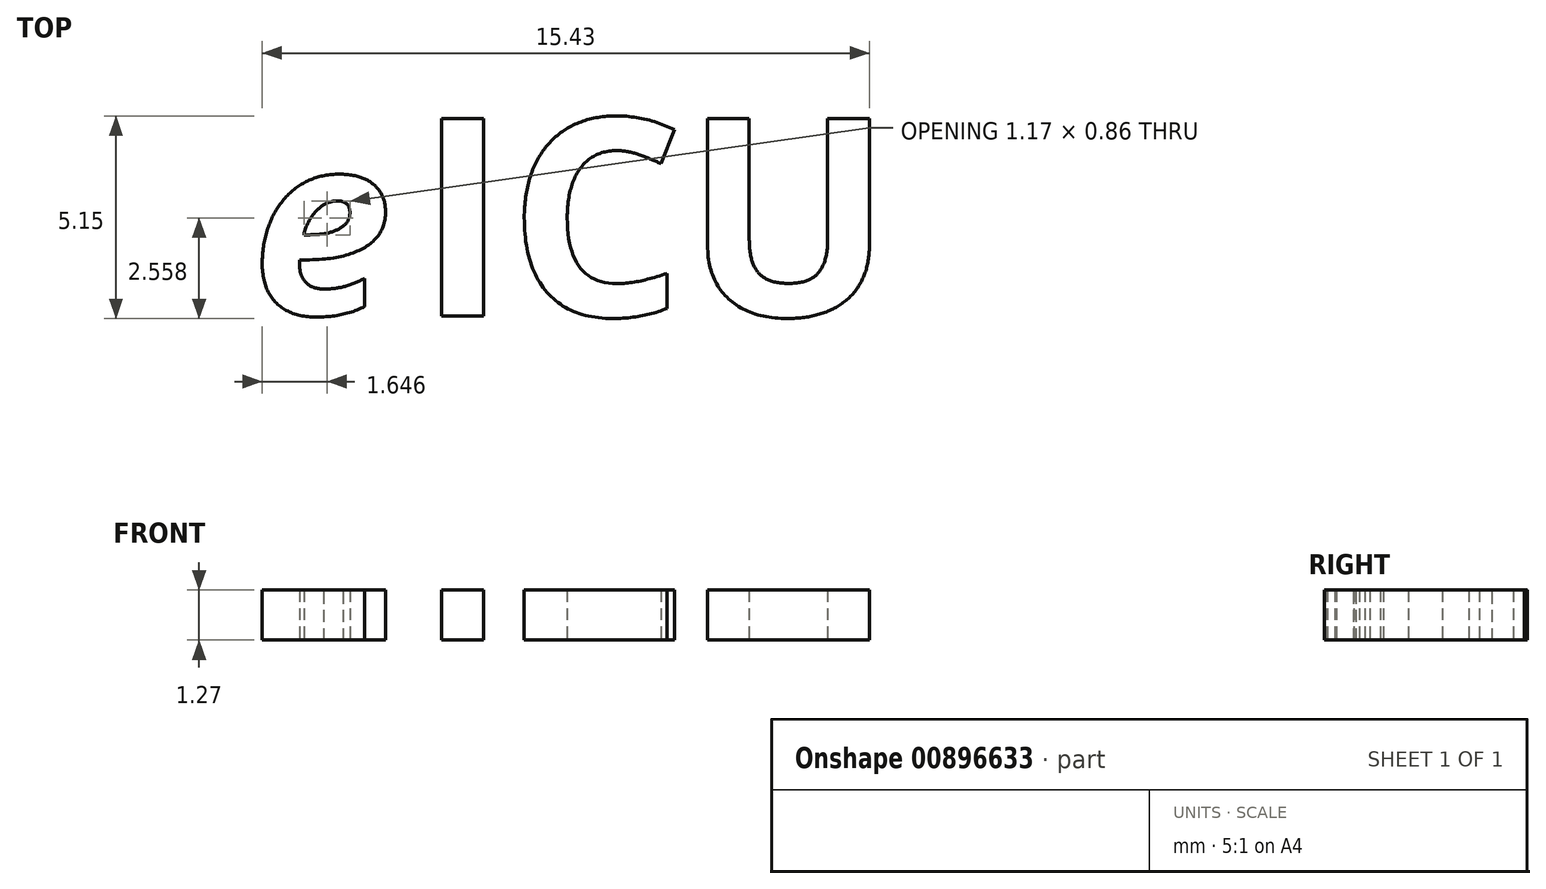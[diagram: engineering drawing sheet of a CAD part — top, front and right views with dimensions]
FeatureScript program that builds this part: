
annotation { "Feature Type Name" : "Feature", "Feature Type Description" : "" }
export const myFeature = defineFeature(function(context is Context, id is Id, definition is map)
    precondition{}
    {
        {
            var Q0;
            Q0=qCreatedBy(makeId("Top.planeOp"),FACE);
            var sketch = newSketch(context, id + "F0", { "sketchPlane" : qUnion([Q0])});
            skText(sketch, "E0", { "text": "ICU", "fontName": "OpenSans-Bold.ttf"});
            skText(sketch, "E1", { "text": "e", "fontName": "OpenSans-BoldItalic.ttf"});
            const initialGuessF0  = {"E0": [0.00421, -3e-05, 1, 0, 0.00505], "E1": [0, 0, 1, 0, 0.00462]};
            skSetInitialGuess(sketch, initialGuessF0);
            skSolve(sketch);
        }
        {
            var Q0;
            Q0 = qSketchRegion(id + "F0", true);
            extrude(context, id + "F1", {"entities" : qUnion([Q0]), "depth" : 1.27 * mm, "offsetDistance" : 25.4 * mm});
        }
    });
